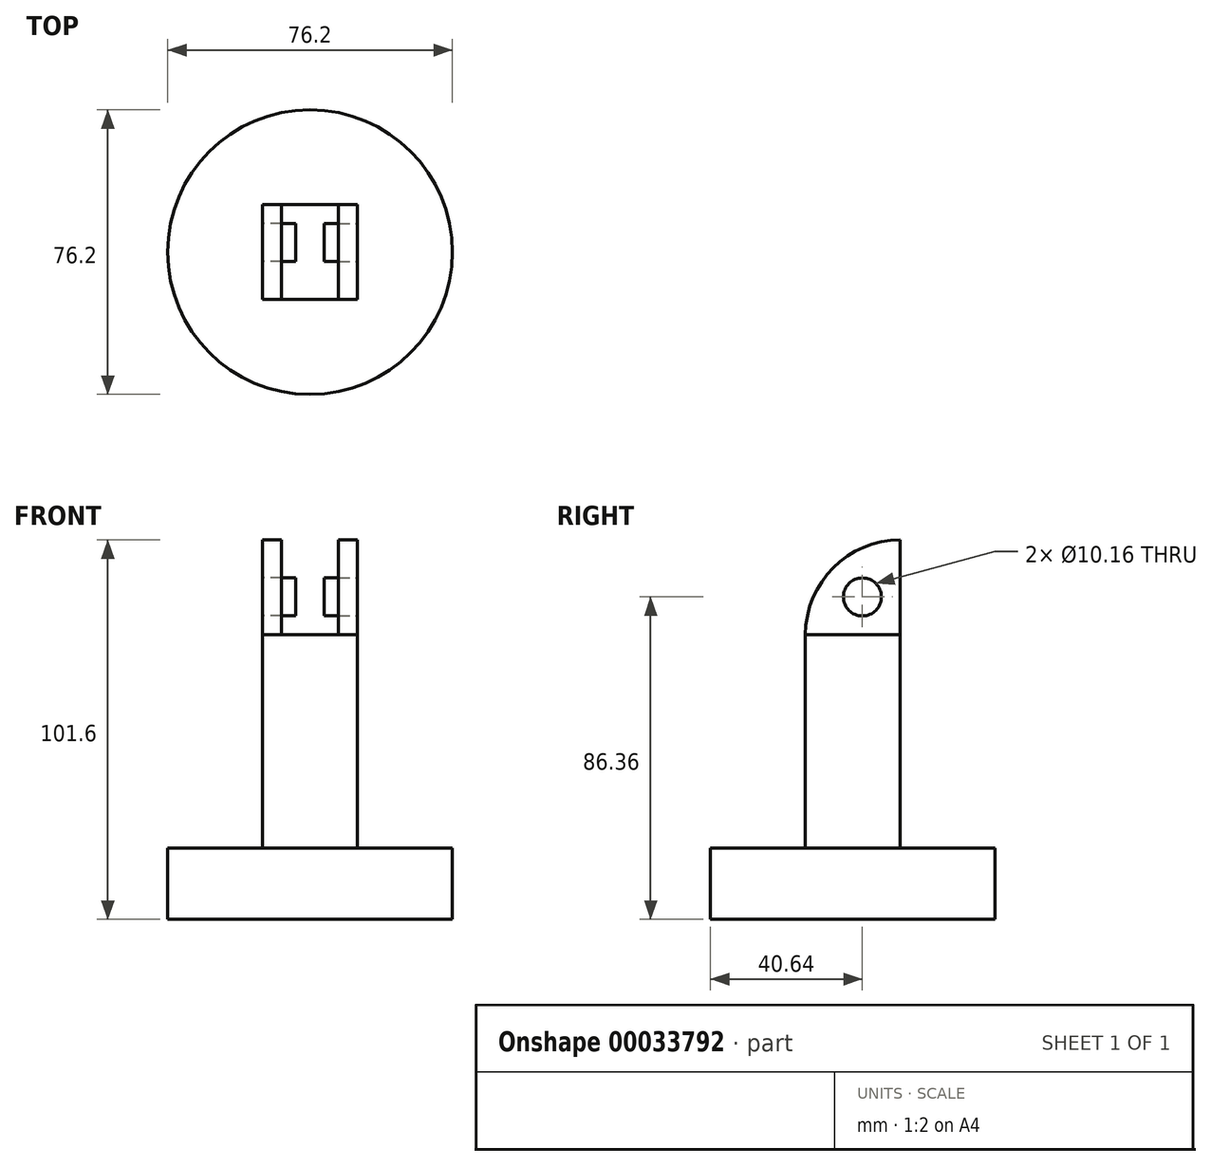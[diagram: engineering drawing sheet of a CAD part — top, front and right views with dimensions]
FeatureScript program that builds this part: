
annotation { "Feature Type Name" : "Feature", "Feature Type Description" : "" }
export const myFeature = defineFeature(function(context is Context, id is Id, definition is map)
    precondition{}
    {
        {
            var Q0;
            Q0=qCreatedBy(makeId("Front.planeOp"),FACE);
            var sketch = newSketch(context, id + "F0", { "sketchPlane" : qUnion([Q0])});
            skLineSegment(sketch, "E0", {"start": v(0, 0) * mm, "end": v(0, 41.58) * mm});
            skLineSegment(sketch, "E1.bottom", {"start": v(0, 0) * mm, "end": v(38.1, 0) * mm});
            skLineSegment(sketch, "E1.top", {"start": v(0, 19.05) * mm, "end": v(38.1, 19.05) * mm});
            skLineSegment(sketch, "E1.left", {"start": v(0, 0) * mm, "end": v(0, 19.05) * mm});
            skLineSegment(sketch, "E1.right", {"start": v(38.1, 0) * mm, "end": v(38.1, 19.05) * mm});
            skSolve(sketch);
        }
        {
            var Q0;
            Q0=makeQuery(id+"F0.imprint","IMPRINT",FACE,{"disambiguationData":[TD([[makeQuery(id+"F0.imprint","IMPRINT",EDGE,{"derivedFrom":sQuery(id+"F0.wireOp",EDGE,"E1.bottom")}),1.0]])]});
            var Q1;
            Q1=sQuery(id+"F0.wireOp",EDGE,"E1.left");
            revolve(context, id + "F1", {"entities" : qUnion([Q0]), "axis" : qUnion([Q1]), "revolveType" : RevolveType.FULL});
        }
        {
            var Q0;
            Q0=qCreatedBy(makeId("Top.planeOp"),FACE);
            var sketch = newSketch(context, id + "F2", { "sketchPlane" : qUnion([Q0])});
            skLineSegment(sketch, "E2.rect.bottom", {"start": v(-12.7, 12.7) * mm, "end": v(12.7, 12.7) * mm});
            skLineSegment(sketch, "E2.rect.top", {"start": v(-12.7, -12.7) * mm, "end": v(12.7, -12.7) * mm});
            skLineSegment(sketch, "E2.rect.left", {"start": v(-12.7, 12.7) * mm, "end": v(-12.7, -12.7) * mm});
            skLineSegment(sketch, "E2.rect.right", {"start": v(12.7, 12.7) * mm, "end": v(12.7, -12.7) * mm});
            skPoint(sketch, "E2.rect.middle", {"position": v(0, 0) * mm});
            skSolve(sketch);
        }
        {
            var Q0;
            Q0 = qSketchRegion(id + "F2", true);
            extrude(context, id + "F3", {"entities" : qUnion([Q0]), "operationType" : NewBodyOperationType.ADD, "depth" : 76.2 * mm});
        }
        {
            var Q0;
            Q0=makeQuery(id+"F3.opExtrude","SWEPT_FACE",FACE,{"disambiguationData":[OSD([sQuery(id+"F2.wireOp",EDGE,"E2.rect.right")])]});
            var sketch = newSketch(context, id + "F4", { "sketchPlane" : qUnion([Q0])});
            skLineSegment(sketch, "E3", {"start": v(12.7, 76.2) * mm, "end": v(12.7, 101.6) * mm});
            skArc(sketch, "E4", {"start": v(12.7, 101.6) * mm, "mid": v(-5.26, 94.16) * mm, "end": v(-12.7, 76.2) * mm});
            skCircle(sketch, "E5", {"center": v(2.54, 86.36) * mm, "radius": 5.08 * mm});
            skSolve(sketch);
        }
        {
            var Q0;
            Q0=makeQuery(id+"F3.opExtrude","SWEPT_FACE",FACE,{"disambiguationData":[OSD([sQuery(id+"F2.wireOp",EDGE,"E2.rect.left")])]});
            var sketch = newSketch(context, id + "F5", { "sketchPlane" : qUnion([Q0])});
            skArc(sketch, "E6", {"start": v(12.7, 76.2) * mm, "mid": v(5.26, 94.16) * mm, "end": v(-12.7, 101.6) * mm});
            skLineSegment(sketch, "E7", {"start": v(-12.7, 76.2) * mm, "end": v(-12.7, 101.6) * mm});
            skCircle(sketch, "E8", {"center": v(-2.54, 86.36) * mm, "radius": 5.08 * mm});
            skSolve(sketch);
        }
        {
            var Q0;
            Q0=makeQuery(id+"F5.imprint","IMPRINT",FACE,{"disambiguationData":[TD([[makeQuery(id+"F5.imprint","IMPRINT",EDGE,{"derivedFrom":sQuery(id+"F5.wireOp",EDGE,"E6")}),1.0]])]});
            extrude(context, id + "F6", {"entities" : qUnion([Q0]), "oppositeDirection" : true, "depth" : 5.08 * mm});
        }
        {
            var Q0;
            Q0=makeQuery(id+"F4.imprint","IMPRINT",FACE,{"disambiguationData":[TD([[makeQuery(id+"F4.imprint","IMPRINT",EDGE,{"derivedFrom":sQuery(id+"F4.wireOp",EDGE,"E3")}),1.0]])]});
            extrude(context, id + "F7", {"entities" : qUnion([Q0]), "oppositeDirection" : true, "depth" : 5.08 * mm});
        }
        {
            var Q0;
            Q0 = qSketchRegion(id + "F4", true);
            extrude(context, id + "F8", {"entities" : qUnion([Q0]), "oppositeDirection" : true, "depth" : 8.9 * mm});
        }
        {
            var Q0;
            Q0=makeQuery(id+"F5.imprint","IMPRINT",FACE,{"disambiguationData":[TD([[makeQuery(id+"F5.imprint","IMPRINT",EDGE,{"derivedFrom":sQuery(id+"F5.wireOp",EDGE,"E8")}),1.0]])]});
            extrude(context, id + "F9", {"entities" : qUnion([Q0]), "oppositeDirection" : true, "depth" : 8.9 * mm});
        }
    });
